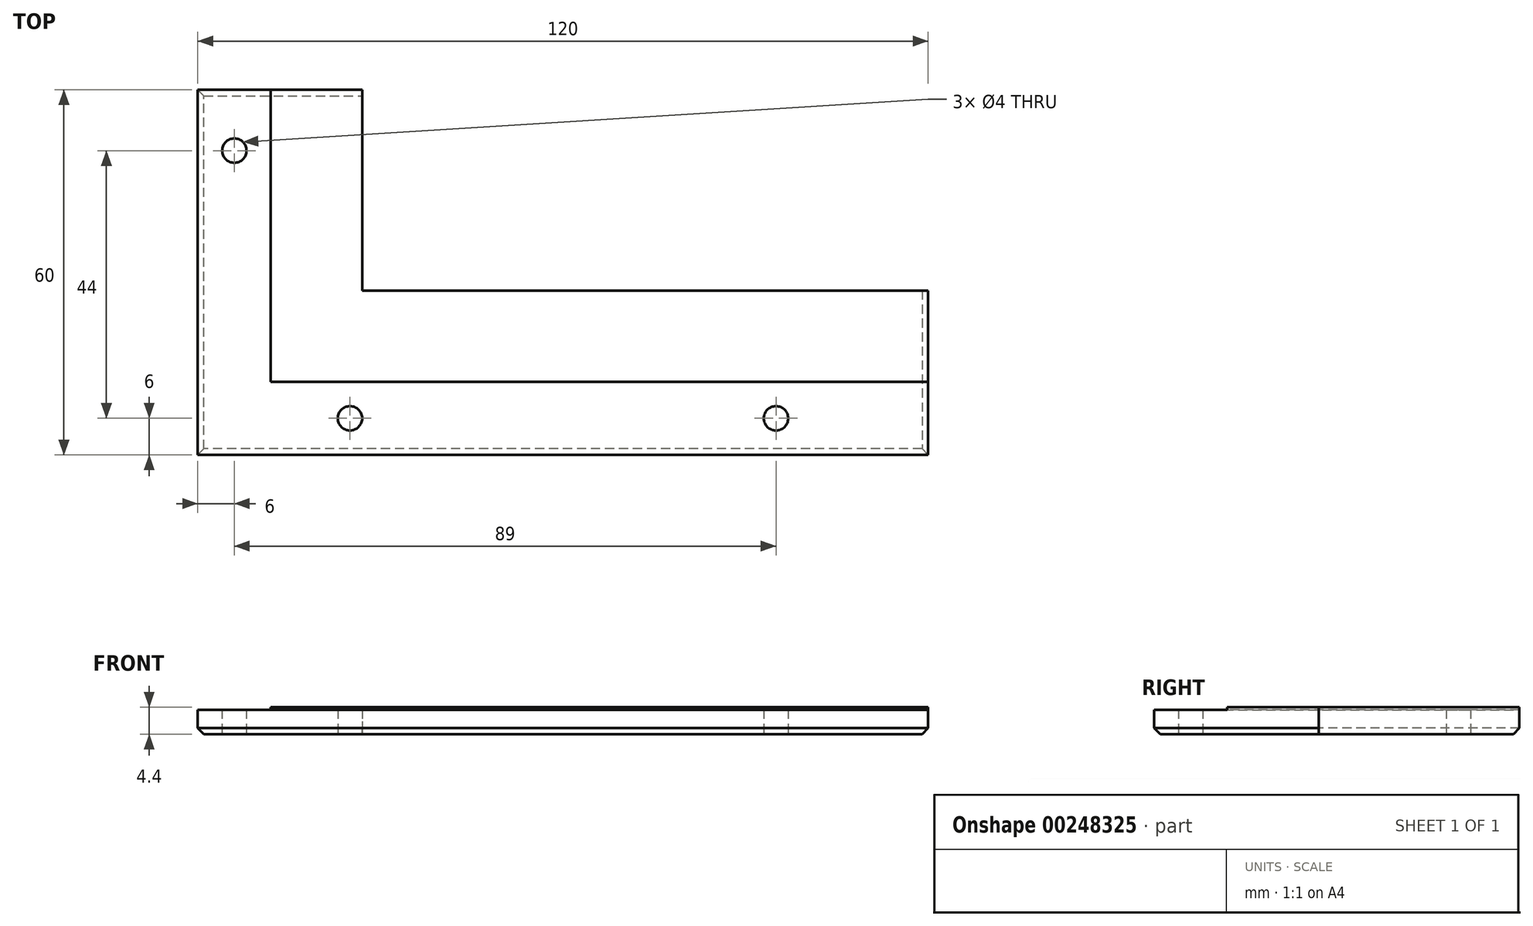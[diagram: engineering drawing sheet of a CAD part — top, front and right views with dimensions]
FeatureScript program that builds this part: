
annotation { "Feature Type Name" : "Feature", "Feature Type Description" : "" }
export const myFeature = defineFeature(function(context is Context, id is Id, definition is map)
    precondition{}
    {
        {
            var Q0;
            Q0=qCreatedBy(makeId("Top.planeOp"),FACE);
            var sketch = newSketch(context, id + "F0", { "sketchPlane" : qUnion([Q0])});
            skLineSegment(sketch, "E0.bottom", {"start": v(0, 0) * mm, "end": v(120, 0) * mm});
            skLineSegment(sketch, "E0.top", {"start": v(0, 60) * mm, "end": v(27, 60) * mm});
            skLineSegment(sketch, "E0.left", {"start": v(0, 0) * mm, "end": v(0, 60) * mm});
            skLineSegment(sketch, "E0.right", {"start": v(120, 0) * mm, "end": v(120, 27) * mm});
            skLineSegment(sketch, "E1", {"start": v(12, 60) * mm, "end": v(12, 12) * mm});
            skLineSegment(sketch, "E2", {"start": v(12, 12) * mm, "end": v(120, 12) * mm});
            skPoint(sketch, "E3.orphan", {"position": v(0, 12) * mm});
            skLineSegment(sketch, "E4", {"start": v(6, 60) * mm, "end": v(6, 0) * mm, "construction": true});
            skLineSegment(sketch, "E5", {"start": v(0, 6) * mm, "end": v(120, 6) * mm, "construction": true});
            skLineSegment(sketch, "E6", {"start": v(-3.03, 50) * mm, "end": v(18.83, 50) * mm, "construction": true});
            skLineSegment(sketch, "E7", {"start": v(25, 12) * mm, "end": v(25, 0) * mm, "construction": true});
            skLineSegment(sketch, "E8", {"start": v(95, 12) * mm, "end": v(95, 0) * mm, "construction": true});
            skCircle(sketch, "E9", {"center": v(6, 50) * mm, "radius": 2 * mm});
            skPoint(sketch, "E9.centerSnap0", {"position": v(7.9, 50) * mm});
            skCircle(sketch, "E10", {"center": v(25, 6) * mm, "radius": 2 * mm});
            skCircle(sketch, "E11", {"center": v(95, 6) * mm, "radius": 2 * mm});
            skLineSegment(sketch, "E12", {"start": v(27, 60) * mm, "end": v(27, 27) * mm});
            skLineSegment(sketch, "E13", {"start": v(27, 27) * mm, "end": v(120, 27) * mm});
            skPoint(sketch, "E14.orphan", {"position": v(27, 12) * mm});
            skSolve(sketch);
        }
        {
            var Q0;
            {var subQ3=sQuery(id+"F0.wireOp",EDGE,"E1");Q0=makeQuery(id+"F0.imprint","IMPRINT",FACE,{"disambiguationData":[TD([[makeQuery(id+"F0.imprint","IMPRINT",EDGE,{"derivedFrom":subQ3}),1.0]])]});}
            var Q1;
            {var subQ1=sQuery(id+"F0.wireOp",EDGE,"E0.bottom");Q1=makeQuery(id+"F0.imprint","IMPRINT",FACE,{"disambiguationData":[TD([[makeQuery(id+"F0.imprint","IMPRINT",EDGE,{"derivedFrom":subQ1}),1.0]])]});}
            extrude(context, id + "F1", {"entities" : qUnion([Q0, Q1]), "depth" : 4 * mm, "offsetDistance" : 25 * mm});
        }
        {
            var Q0;
            Q0=makeQuery(id+"F1.opExtrude","CAP_FACE",FACE,{"disambiguationData":[OSD([sQuery(id+"F0.wireOp",EDGE,"E0.bottom"),sQuery(id+"F0.wireOp",EDGE,"E0.top"),sQuery(id+"F0.wireOp",EDGE,"E0.left"),sQuery(id+"F0.wireOp",EDGE,"E0.right"),sQuery(id+"F0.wireOp",EDGE,"E9"),sQuery(id+"F0.wireOp",EDGE,"E10"),sQuery(id+"F0.wireOp",EDGE,"E11")])],"isStart":false});
            var sketch = newSketch(context, id + "F2", { "sketchPlane" : qUnion([Q0])});
            skLineSegment(sketch, "E15.0", {"start": v(12, 60) * mm, "end": v(12, 12) * mm});
            skLineSegment(sketch, "E16.0", {"start": v(12, 12) * mm, "end": v(120, 12) * mm});
            skSolve(sketch);
        }
        {
            var Q0;
            Q0 = qSketchRegion(id + "F2", true);
            var Q1;
            {var subQ0=sQuery(id+"F2.wireOp",EDGE,"E15.0");Q1=makeQuery(id+"F2.imprint","IMPRINT",FACE,{"disambiguationData":[TD([[makeQuery(id+"F2.imprint","IMPRINT",EDGE,{"derivedFrom":subQ0}),1.0]])]});}
            extrude(context, id + "F3", {"entities" : qUnion([Q0, Q1]), "operationType" : NewBodyOperationType.ADD, "depth" : 0.4 * mm, "offsetDistance" : 25 * mm});
        }
        {
            var Q0;
            Q0=makeQuery(id+"F1.opExtrude","CAP_EDGE",EDGE,{"disambiguationData":[OSD([sQuery(id+"F0.wireOp",EDGE,"E0.right")])],"isStart":true});
            var Q1;
            Q1=makeQuery(id+"F1.opExtrude","CAP_EDGE",EDGE,{"disambiguationData":[OSD([sQuery(id+"F0.wireOp",EDGE,"E0.top")])],"isStart":true});
            var Q2;
            Q2=makeQuery(id+"F1.opExtrude","CAP_EDGE",EDGE,{"disambiguationData":[OSD([sQuery(id+"F0.wireOp",EDGE,"E0.bottom")])],"isStart":true});
            var Q3;
            Q3=makeQuery(id+"F1.opExtrude","CAP_EDGE",EDGE,{"disambiguationData":[OSD([sQuery(id+"F0.wireOp",EDGE,"E0.left")])],"isStart":true});
            chamfer(context, id + "F4", {"entities" : qUnion([Q0, Q1, Q2, Q3]), "width" : 1 * mm, "tangentPropagation" : true});
        }
    });
